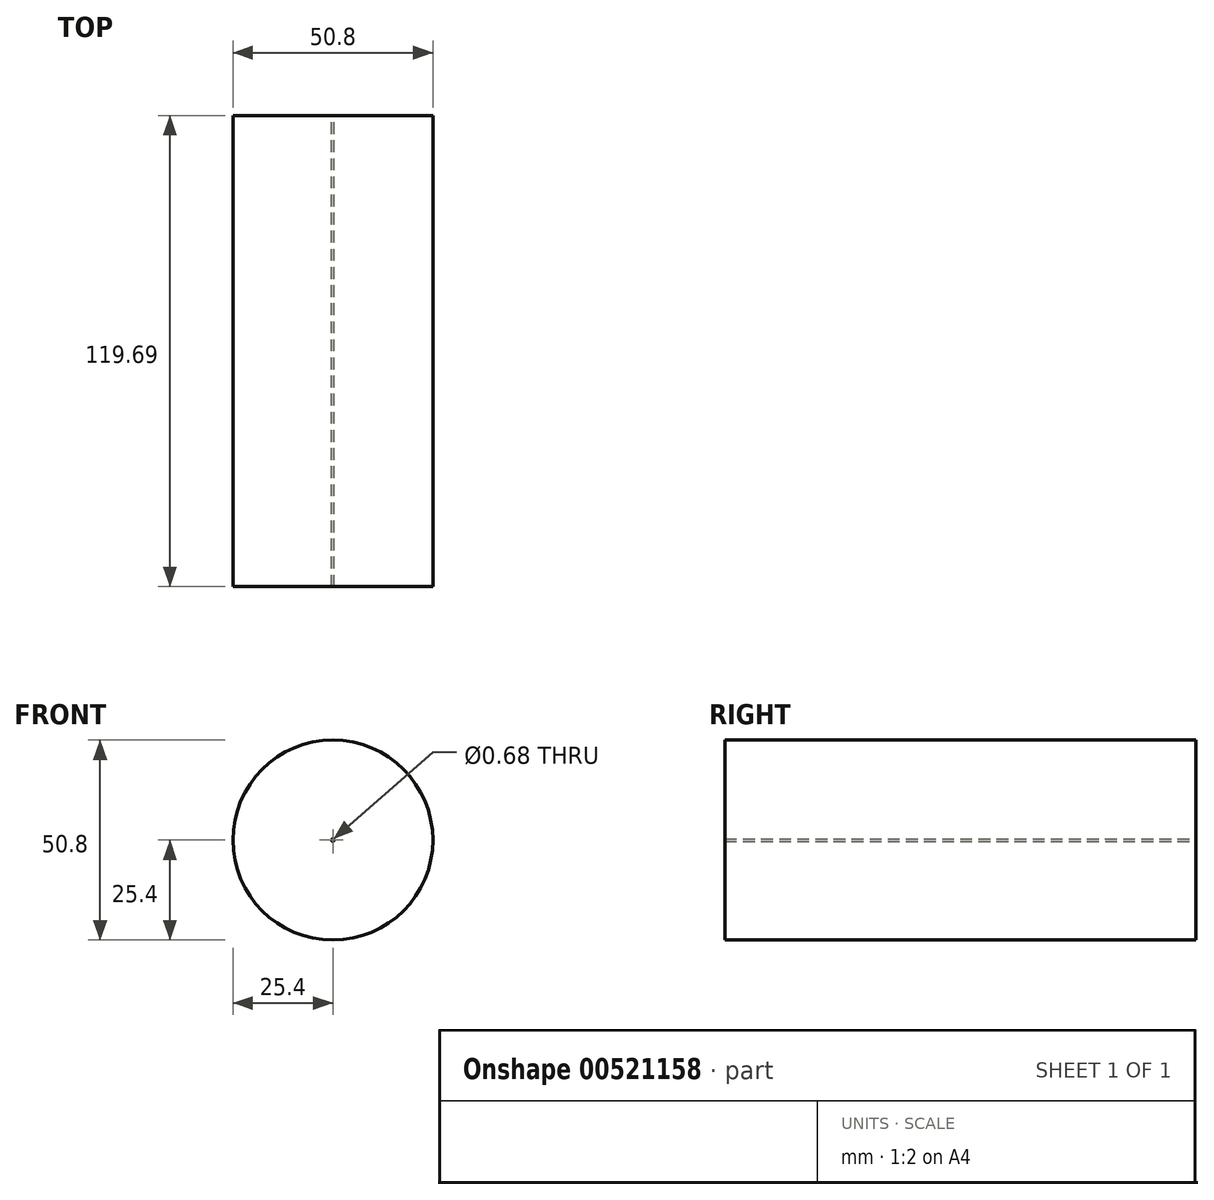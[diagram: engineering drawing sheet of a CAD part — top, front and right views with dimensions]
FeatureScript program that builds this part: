
annotation { "Feature Type Name" : "Feature", "Feature Type Description" : "" }
export const myFeature = defineFeature(function(context is Context, id is Id, definition is map)
    precondition{}
    {
        {
            var Q0;
            Q0=qCreatedBy(makeId("Front.planeOp"),FACE);
            var sketch = newSketch(context, id + "F0", { "sketchPlane" : qUnion([Q0])});
            skCircle(sketch, "E0", {"center": v(0, 0) * mm, "radius": 0.34 * mm});
            skCircle(sketch, "E1", {"center": v(0, 0) * mm, "radius": 25.4 * mm});
            skSolve(sketch);
        }
        {
            var Q0;
            Q0 = qSketchRegion(id + "F0", true);
            extrude(context, id + "F1", {"entities" : qUnion([Q0]), "depth" : 119.69 * mm, "offsetDistance" : 25.4 * mm});
        }
    });
